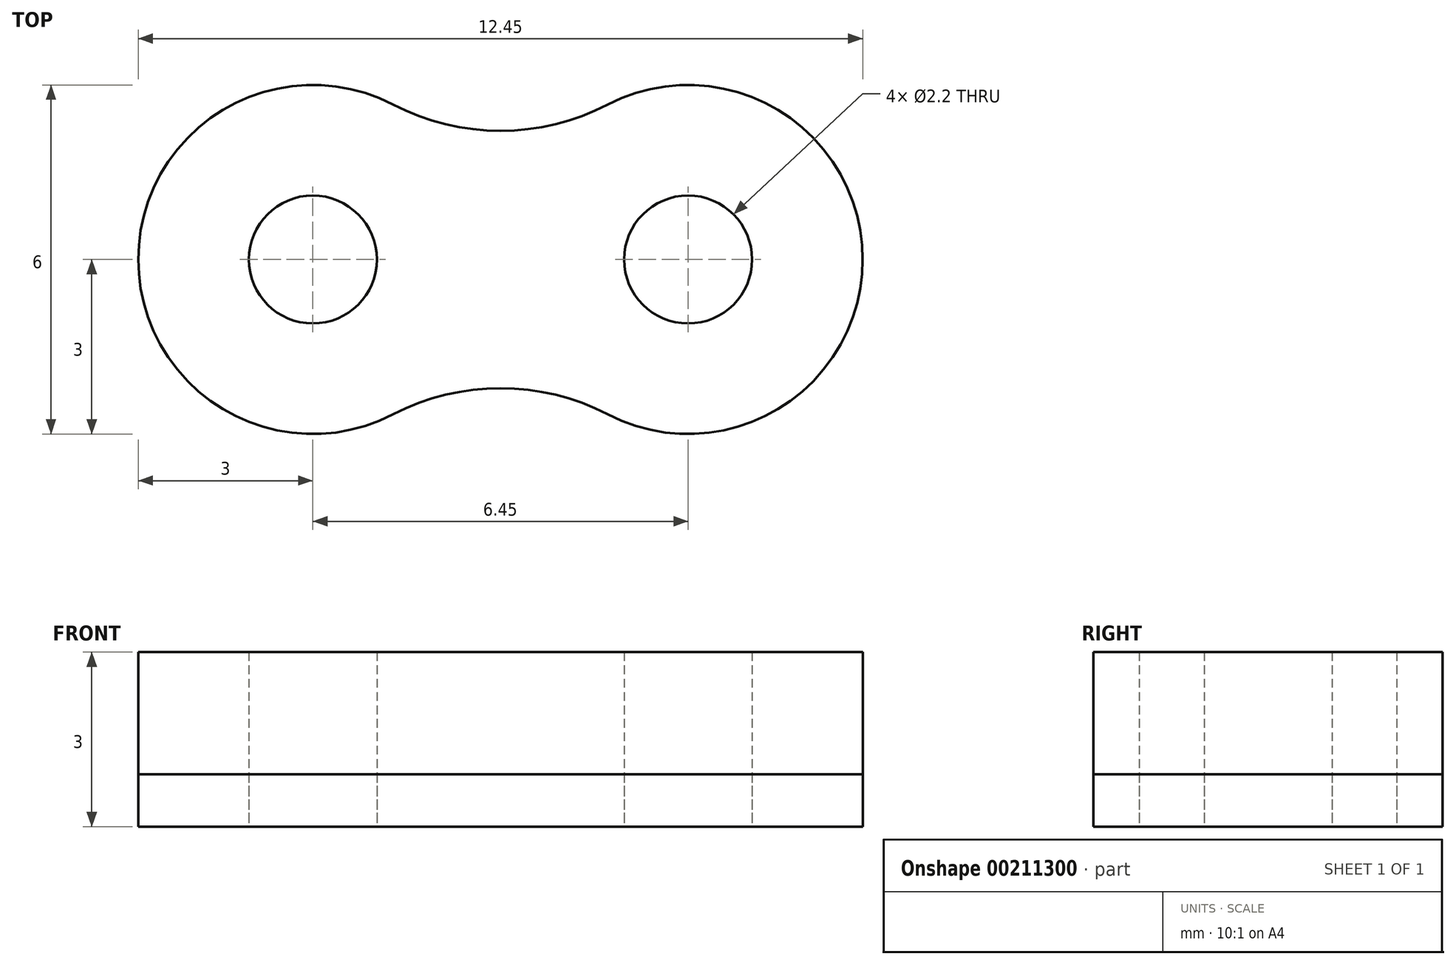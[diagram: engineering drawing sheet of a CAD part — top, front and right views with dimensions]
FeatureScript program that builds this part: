
annotation { "Feature Type Name" : "Feature", "Feature Type Description" : "" }
export const myFeature = defineFeature(function(context is Context, id is Id, definition is map)
    precondition{}
    {
        {
            var Q0;
            Q0=qCreatedBy(makeId("Top.planeOp"),FACE);
            var sketch = newSketch(context, id + "F0", { "sketchPlane" : qUnion([Q0])});
            skCircle(sketch, "E0", {"center": v(0, 0) * mm, "radius": 3 * mm});
            skCircle(sketch, "E1", {"center": v(6.45, 0) * mm, "radius": 3 * mm});
            skCircle(sketch, "E2", {"center": v(0, 0) * mm, "radius": 1.1 * mm});
            skCircle(sketch, "E3", {"center": v(6.45, 0) * mm, "radius": 1.1 * mm});
            skArc(sketch, "E4", {"start": v(1.38, 2.66) * mm, "mid": v(3.23, 2.21) * mm, "end": v(5.07, 2.66) * mm});
            skArc(sketch, "E5.MirrorCS", {"start": v(1.38, -2.66) * mm, "mid": v(3.23, -2.21) * mm, "end": v(5.07, -2.66) * mm});
            skSolve(sketch);
        }
        {
            var Q0;
            Q0=makeQuery(id+"F0.imprint","IMPRINT",FACE,{"disambiguationData":[TD([[makeQuery(id+"F0.imprint","IMPRINT",EDGE,{"derivedFrom":sQuery(id+"F0.wireOp",EDGE,"E3")}),-1.0]])]});
            var Q1;
            Q1=makeQuery(id+"F0.imprint","IMPRINT",FACE,{"disambiguationData":[TD([[makeQuery(id+"F0.imprint","IMPRINT",EDGE,{"derivedFrom":sQuery(id+"F0.wireOp",EDGE,"E2")}),-1.0]])]});
            var Q2;
            {var subQ0=sQuery(id+"F0.wireOp",EDGE,"E4");Q2=makeQuery(id+"F0.imprint","IMPRINT",FACE,{"disambiguationData":[TD([[makeQuery(id+"F0.imprint","IMPRINT",EDGE,{"derivedFrom":subQ0}),-1.0]])]});}
            var Q3;
            {var subQ0=sQuery(id+"F0.wireOp",EDGE,"E5.MirrorCS");Q3=makeQuery(id+"F0.imprint","IMPRINT",FACE,{"disambiguationData":[TD([[makeQuery(id+"F0.imprint","IMPRINT",EDGE,{"derivedFrom":subQ0}),1.0]])]});}
            extrude(context, id + "F1", {"entities" : qUnion([Q0, Q1, Q2, Q3]), "depth" : 0.9 * mm});
        }
        {
            var Q0;
            Q0 = qSketchRegion(id + "F0", true);
            extrude(context, id + "F2", {"entities" : qUnion([Q0]), "depth" : 3 * mm});
        }
    });
